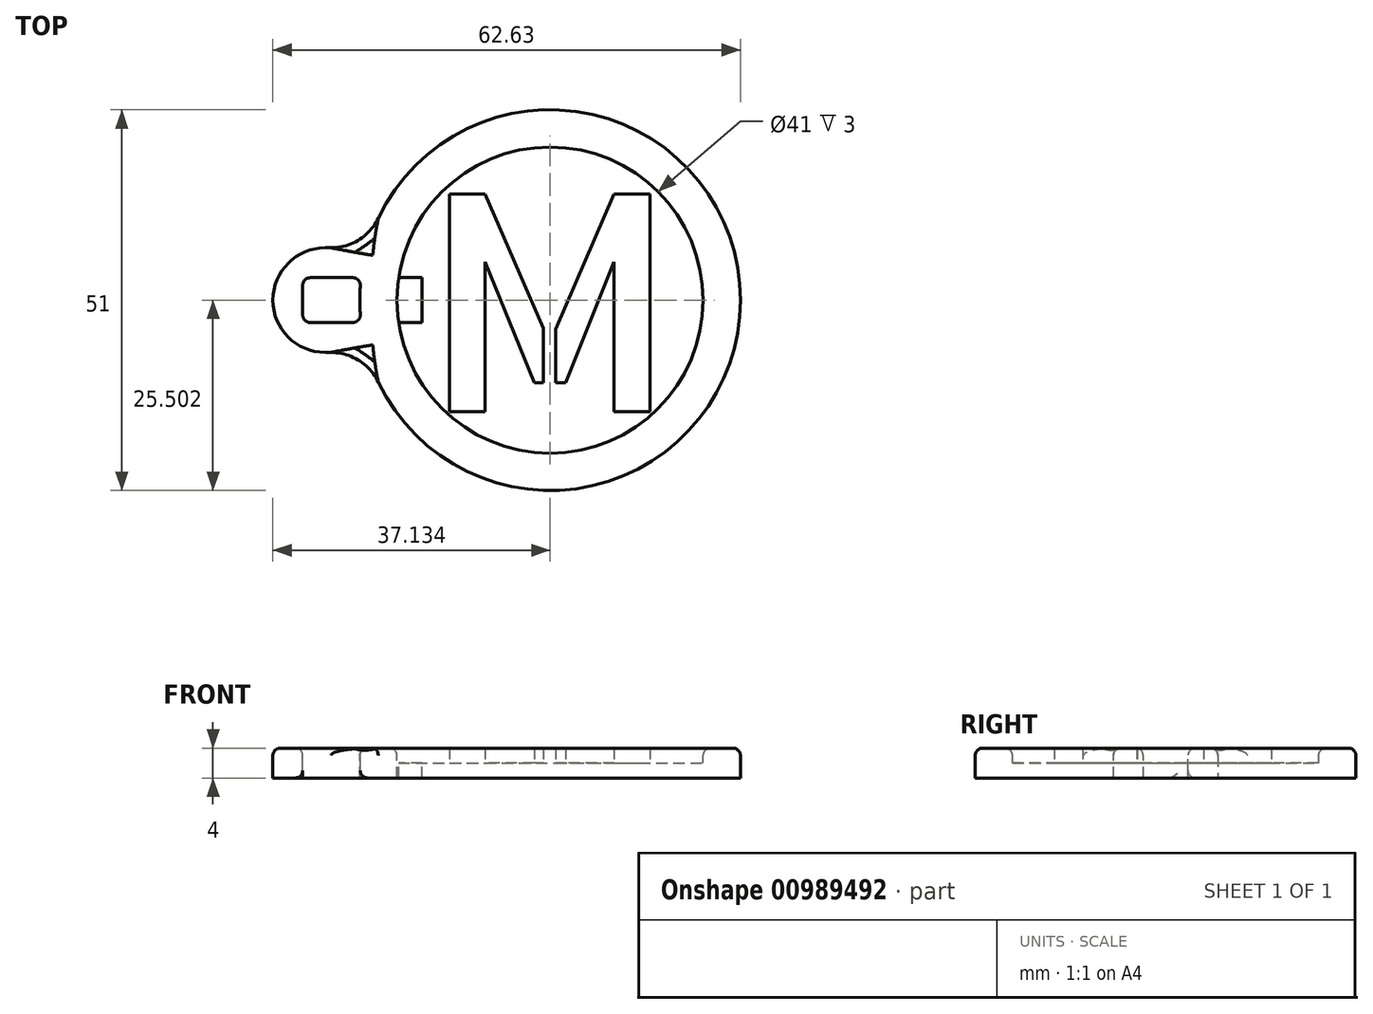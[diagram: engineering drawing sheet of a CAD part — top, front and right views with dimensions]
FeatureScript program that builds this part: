
annotation { "Feature Type Name" : "Feature", "Feature Type Description" : "" }
export const myFeature = defineFeature(function(context is Context, id is Id, definition is map)
    precondition{}
    {
        {
            var Q0;
            Q0=qCreatedBy(makeId("Top.planeOp"),FACE);
            var sketch = newSketch(context, id + "F0", { "sketchPlane" : qUnion([Q0])});
            skText(sketch, "E0", { "text": "M", "fontName": "AllertaStencil-Regular.ttf"});
            skCircle(sketch, "E1", {"center": v(17.13, 14.92) * mm, "radius": 20.5 * mm});
            skPoint(sketch, "E1.centerSnap0", {"position": v(16.61, 14.92) * mm});
            skCircle(sketch, "E2", {"center": v(17.13, 14.92) * mm, "radius": 25.5 * mm});
            skLineSegment(sketch, "E3.bottom", {"start": v(0, 7.92) * mm, "end": v(-20, 7.92) * mm});
            skLineSegment(sketch, "E3.top", {"start": v(0, 21.92) * mm, "end": v(-20, 21.92) * mm});
            skLineSegment(sketch, "E3.left", {"start": v(0, 7.92) * mm, "end": v(0, 21.92) * mm});
            skLineSegment(sketch, "E3.right", {"start": v(-20, 7.92) * mm, "end": v(-20, 21.92) * mm});
            skLineSegment(sketch, "E4.bottom", {"start": v(0, 11.92) * mm, "end": v(-16, 11.92) * mm});
            skLineSegment(sketch, "E4.top", {"start": v(0, 17.92) * mm, "end": v(-16, 17.92) * mm});
            skLineSegment(sketch, "E4.left", {"start": v(0, 11.92) * mm, "end": v(0, 17.92) * mm});
            skLineSegment(sketch, "E4.right", {"start": v(-16, 11.92) * mm, "end": v(-16, 17.92) * mm});
            const initialGuessF0  = {"E0": [0, 0, 1, 0, 0.02911]};
            skSetInitialGuess(sketch, initialGuessF0);
            skSolve(sketch);
        }
        {
            var Q0;
            {var subQ0=sQuery(id+"F0.wireOp",EDGE,"E3.top");var subQ1=sQuery(id+"F0.wireOp",EDGE,"E1");var subQ2=makeQuery(id+"F0.imprint","INTERSECT",VERTEX,{"derivedFrom":[subQ1,subQ0]});Q0=makeQuery(id+"F0.imprint","IMPRINT",FACE,{"disambiguationData":[TD([[makeQuery(id+"F0.imprint","IMPRINT",EDGE,{"disambiguationData":[TD([[subQ2,1.0]])],"derivedFrom":subQ1}),-1.0]])]});}
            var Q1;
            {var subQ0=sQuery(id+"F0.wireOp",EDGE,"E4.top");var subQ1=sQuery(id+"F0.wireOp",EDGE,"E1");var subQ2=makeQuery(id+"F0.imprint","INTERSECT",VERTEX,{"derivedFrom":[subQ1,subQ0]});Q1=makeQuery(id+"F0.imprint","IMPRINT",FACE,{"disambiguationData":[TD([[makeQuery(id+"F0.imprint","IMPRINT",EDGE,{"disambiguationData":[TD([[subQ2,1.0]])],"derivedFrom":subQ1}),-1.0]])]});}
            var Q2;
            {var subQ0=sQuery(id+"F0.wireOp",EDGE,"E4.top");var subQ1=sQuery(id+"F0.wireOp",EDGE,"E1");var subQ2=makeQuery(id+"F0.imprint","INTERSECT",VERTEX,{"derivedFrom":[subQ1,subQ0]});Q2=makeQuery(id+"F0.imprint","IMPRINT",FACE,{"disambiguationData":[TD([[makeQuery(id+"F0.imprint","IMPRINT",EDGE,{"disambiguationData":[TD([[subQ2,-1.0]])],"derivedFrom":subQ1}),-1.0]])]});}
            var Q3;
            {var subQ0=sQuery(id+"F0.wireOp",EDGE,"E4.bottom");var subQ1=sQuery(id+"F0.wireOp",EDGE,"E1");var subQ2=makeQuery(id+"F0.imprint","INTERSECT",VERTEX,{"derivedFrom":[subQ1,subQ0]});Q3=makeQuery(id+"F0.imprint","IMPRINT",FACE,{"disambiguationData":[TD([[makeQuery(id+"F0.imprint","IMPRINT",EDGE,{"disambiguationData":[TD([[subQ2,-1.0]])],"derivedFrom":subQ1}),-1.0]])]});}
            var Q4;
            {var subQ0=sQuery(id+"F0.wireOp",EDGE,"E3.right");Q4=makeQuery(id+"F0.imprint","IMPRINT",FACE,{"disambiguationData":[TD([[makeQuery(id+"F0.imprint","IMPRINT",EDGE,{"derivedFrom":subQ0}),-1.0]])]});}
            var Q5;
            {var subQ5=sQuery(id+"F0.wireOp",EDGE,"E4.left");Q5=makeQuery(id+"F0.imprint","IMPRINT",FACE,{"disambiguationData":[TD([[makeQuery(id+"F0.imprint","IMPRINT",EDGE,{"derivedFrom":subQ5}),1.0]])]});}
            var Q6;
            {var subQ0=sQuery(id+"F0.wireOp",EDGE,"E4.top");var subQ1=sQuery(id+"F0.wireOp",EDGE,"E1");var subQ2=makeQuery(id+"F0.imprint","INTERSECT",VERTEX,{"derivedFrom":[subQ1,subQ0]});Q6=makeQuery(id+"F0.imprint","IMPRINT",FACE,{"disambiguationData":[TD([[makeQuery(id+"F0.imprint","IMPRINT",EDGE,{"disambiguationData":[TD([[subQ2,1.0]])],"derivedFrom":subQ1}),1.0]])]});}
            var Q7;
            {var subQ0=sQuery(id+"F0.wireOp",EDGE,"E4.bottom");var subQ1=sQuery(id+"F0.wireOp",EDGE,"E1");var subQ2=makeQuery(id+"F0.imprint","INTERSECT",VERTEX,{"derivedFrom":[subQ1,subQ0]});Q7=makeQuery(id+"F0.imprint","IMPRINT",FACE,{"disambiguationData":[TD([[makeQuery(id+"F0.imprint","IMPRINT",EDGE,{"disambiguationData":[TD([[subQ2,-1.0]])],"derivedFrom":subQ1}),1.0]])]});}
            var Q8;
            Q8=makeQuery(id+"F0.imprint","IMPRINT",FACE,{"disambiguationData":[TD([[makeQuery(id+"F0.imprint","IMPRINT",EDGE,{"derivedFrom":sQuery(id+"F0.wireOp",EDGE,"E0.sketch_text.stroke-0")}),1.0]])]});
            var Q9;
            Q9=makeQuery(id+"F0.imprint","IMPRINT",FACE,{"disambiguationData":[TD([[makeQuery(id+"F0.imprint","IMPRINT",EDGE,{"derivedFrom":sQuery(id+"F0.wireOp",EDGE,"E0.sketch_text.stroke-0")}),-1.0]])]});
            var Q10;
            Q10=makeQuery(id+"F0.imprint","IMPRINT",FACE,{"disambiguationData":[TD([[makeQuery(id+"F0.imprint","IMPRINT",EDGE,{"derivedFrom":sQuery(id+"F0.wireOp",EDGE,"E0.sketch_text.stroke-8")}),-1.0]])]});
            var Q11;
            {var subQ0=sQuery(id+"F0.wireOp",EDGE,"wxvuEN93-N0YH-PEau-rIz5-DYCHeZqUycJo");var subQ1=sQuery(id+"F0.wireOp",EDGE,"E1");var subQ2=makeQuery(id+"F0.imprint","INTERSECT",VERTEX,{"derivedFrom":[subQ1,subQ0]});Q11=makeQuery(id+"F0.imprint","IMPRINT",FACE,{"disambiguationData":[TD([[makeQuery(id+"F0.imprint","IMPRINT",EDGE,{"disambiguationData":[TD([[subQ2,-1.0]])],"derivedFrom":subQ1}),-1.0]])]});}
            var Q12;
            {var subQ4=sQuery(id+"F0.wireOp",EDGE,"E0.sketch_text.stroke-2");Q12=makeQuery(id+"F0.imprint","IMPRINT",FACE,{"disambiguationData":[TD([[makeQuery(id+"F0.imprint","IMPRINT",EDGE,{"derivedFrom":subQ4}),-1.0]])]});}
            var Q13;
            {var subQ0=sQuery(id+"F0.wireOp",EDGE,"E0.sketch_text.stroke-5");var subQ1=sQuery(id+"F0.wireOp",EDGE,"E0.sketch_text.stroke-4");var subQ2=makeQuery(id+"F0.imprint","INTERSECT",VERTEX,{"derivedFrom":[subQ1,subQ0]});Q13=makeQuery(id+"F0.imprint","IMPRINT",FACE,{"disambiguationData":[TD([[makeQuery(id+"F0.imprint","IMPRINT",EDGE,{"disambiguationData":[TD([[subQ2,1.0]])],"derivedFrom":subQ1}),1.0]])]});}
            var Q14;
            {var subQ5=sQuery(id+"F0.wireOp",EDGE,"E0.sketch_text.stroke-6");var subQ7=sQuery(id+"F0.wireOp",EDGE,"E0.sketch_text.stroke-5");var subQ8=makeQuery(id+"F0.imprint","INTERSECT",VERTEX,{"derivedFrom":[subQ7,subQ5]});Q14=makeQuery(id+"F0.imprint","IMPRINT",FACE,{"disambiguationData":[TD([[makeQuery(id+"F0.imprint","IMPRINT",EDGE,{"disambiguationData":[TD([[subQ8,1.0]])],"derivedFrom":subQ7}),-1.0]])]});}
            var Q15;
            {var subQ5=sQuery(id+"F0.wireOp",EDGE,"E1");var subQ7=sQuery(id+"F0.wireOp",EDGE,"E0.sketch_text.stroke-7");var subQ8=makeQuery(id+"F0.imprint","INTERSECT",VERTEX,{"derivedFrom":[subQ7,subQ5]});Q15=makeQuery(id+"F0.imprint","IMPRINT",FACE,{"disambiguationData":[TD([[makeQuery(id+"F0.imprint","IMPRINT",EDGE,{"disambiguationData":[TD([[subQ8,-1.0]])],"derivedFrom":subQ7}),1.0]])]});}
            extrude(context, id + "F1", {"entities" : qUnion([Q0, Q1, Q2, Q3, Q4, Q5, Q6, Q7, Q8, Q9, Q10, Q11, Q12, Q13, Q14, Q15]), "oppositeDirection" : true, "depth" : 2 * mm, "offsetDistance" : 25 * mm});
        }
        {
            var Q0;
            Q0=makeQuery(id+"F0.imprint","IMPRINT",FACE,{"disambiguationData":[TD([[makeQuery(id+"F0.imprint","IMPRINT",EDGE,{"derivedFrom":sQuery(id+"F0.wireOp",EDGE,"E0.sketch_text.stroke-8")}),-1.0]])]});
            var Q1;
            Q1=makeQuery(id+"F0.imprint","IMPRINT",FACE,{"disambiguationData":[TD([[makeQuery(id+"F0.imprint","IMPRINT",EDGE,{"derivedFrom":sQuery(id+"F0.wireOp",EDGE,"E0.sketch_text.stroke-0")}),-1.0]])]});
            var Q2;
            {var subQ0=sQuery(id+"F0.wireOp",EDGE,"E3.top");var subQ1=sQuery(id+"F0.wireOp",EDGE,"E1");var subQ2=makeQuery(id+"F0.imprint","INTERSECT",VERTEX,{"derivedFrom":[subQ1,subQ0]});Q2=makeQuery(id+"F0.imprint","IMPRINT",FACE,{"disambiguationData":[TD([[makeQuery(id+"F0.imprint","IMPRINT",EDGE,{"disambiguationData":[TD([[subQ2,1.0]])],"derivedFrom":subQ1}),-1.0]])]});}
            var Q3;
            {var subQ0=sQuery(id+"F0.wireOp",EDGE,"E4.top");var subQ1=sQuery(id+"F0.wireOp",EDGE,"E1");var subQ2=makeQuery(id+"F0.imprint","INTERSECT",VERTEX,{"derivedFrom":[subQ1,subQ0]});Q3=makeQuery(id+"F0.imprint","IMPRINT",FACE,{"disambiguationData":[TD([[makeQuery(id+"F0.imprint","IMPRINT",EDGE,{"disambiguationData":[TD([[subQ2,1.0]])],"derivedFrom":subQ1}),-1.0]])]});}
            var Q4;
            {var subQ0=sQuery(id+"F0.wireOp",EDGE,"E4.top");var subQ1=sQuery(id+"F0.wireOp",EDGE,"E1");var subQ2=makeQuery(id+"F0.imprint","INTERSECT",VERTEX,{"derivedFrom":[subQ1,subQ0]});Q4=makeQuery(id+"F0.imprint","IMPRINT",FACE,{"disambiguationData":[TD([[makeQuery(id+"F0.imprint","IMPRINT",EDGE,{"disambiguationData":[TD([[subQ2,-1.0]])],"derivedFrom":subQ1}),-1.0]])]});}
            var Q5;
            {var subQ0=sQuery(id+"F0.wireOp",EDGE,"E4.bottom");var subQ1=sQuery(id+"F0.wireOp",EDGE,"E1");var subQ2=makeQuery(id+"F0.imprint","INTERSECT",VERTEX,{"derivedFrom":[subQ1,subQ0]});Q5=makeQuery(id+"F0.imprint","IMPRINT",FACE,{"disambiguationData":[TD([[makeQuery(id+"F0.imprint","IMPRINT",EDGE,{"disambiguationData":[TD([[subQ2,-1.0]])],"derivedFrom":subQ1}),-1.0]])]});}
            var Q6;
            {var subQ0=sQuery(id+"F0.wireOp",EDGE,"E3.right");Q6=makeQuery(id+"F0.imprint","IMPRINT",FACE,{"disambiguationData":[TD([[makeQuery(id+"F0.imprint","IMPRINT",EDGE,{"derivedFrom":subQ0}),-1.0]])]});}
            extrude(context, id + "F2", {"entities" : qUnion([Q0, Q1, Q2, Q3, Q4, Q5, Q6]), "operationType" : NewBodyOperationType.ADD, "depth" : 2 * mm, "offsetDistance" : 25 * mm});
        }
        {
            var Q0;
            Q0=makeQuery(id+"F2.opExtrude","CAP_FACE",FACE,{"disambiguationData":[OSD([sQuery(id+"F0.wireOp",EDGE,"E1"),sQuery(id+"F0.wireOp",EDGE,"E2"),sQuery(id+"F0.wireOp",EDGE,"E3.bottom"),sQuery(id+"F0.wireOp",EDGE,"E3.top"),sQuery(id+"F0.wireOp",EDGE,"E3.right"),sQuery(id+"F0.wireOp",EDGE,"E4.bottom"),sQuery(id+"F0.wireOp",EDGE,"E4.top"),sQuery(id+"F0.wireOp",EDGE,"E4.right")])],"isStart":false});
            var Q1;
            Q1=makeQuery(id+"F2.opExtrude","CAP_EDGE",EDGE,{"disambiguationData":[OSD([sQuery(id+"F0.wireOp",EDGE,"E4.top")])],"isStart":false});
            var Q2;
            {var subQ0=sQuery(id+"F0.wireOp",EDGE,"E4.top");Q2=makeQuery(id+"F2.boolean.opBoolean","MERGE",FACE,{"derivedFrom":[makeQuery(id+"F1.opExtrude","SWEPT_FACE",FACE,{"disambiguationData":[OSD([subQ0])]}),makeQuery(id+"F2.opExtrude","SWEPT_FACE",FACE,{"disambiguationData":[OSD([subQ0])]})]});}
            var Q3;
            {var subQ0=sQuery(id+"F0.wireOp",EDGE,"E4.bottom");var subQ1=sQuery(id+"F0.wireOp",EDGE,"E2");Q3=makeQuery(id+"F2.boolean.opBoolean","MERGE",EDGE,{"derivedFrom":[makeQuery(id+"F1.opExtrude","SWEPT_EDGE",EDGE,{"disambiguationData":[OSD([subQ1,subQ0])]}),makeQuery(id+"F2.opExtrude","SWEPT_EDGE",EDGE,{"disambiguationData":[OSD([subQ1,subQ0])]})]});}
            var Q4;
            {var subQ0=sQuery(id+"F0.wireOp",EDGE,"E4.right");var subQ1=sQuery(id+"F0.wireOp",EDGE,"E4.bottom");Q4=makeQuery(id+"F2.boolean.opBoolean","MERGE",EDGE,{"derivedFrom":[makeQuery(id+"F1.opExtrude","SWEPT_EDGE",EDGE,{"disambiguationData":[OSD([subQ1,subQ0])]}),makeQuery(id+"F2.opExtrude","SWEPT_EDGE",EDGE,{"disambiguationData":[OSD([subQ1,subQ0])]})]});}
            fillet(context, id + "F3", {"entities" : qUnion([Q0, Q1, Q2, Q3, Q4]), "radius" : 1 * mm, "tangentPropagation" : true, "allowEdgeOverflow" : false});
        }
        {
            var Q0;
            {var subQ0=sQuery(id+"F0.wireOp",EDGE,"E3.right");var subQ1=sQuery(id+"F0.wireOp",EDGE,"E3.bottom");Q0=makeQuery(id+"F2.boolean.opBoolean","MERGE",EDGE,{"derivedFrom":[makeQuery(id+"F1.opExtrude","SWEPT_EDGE",EDGE,{"disambiguationData":[OSD([subQ1,subQ0])]}),makeQuery(id+"F2.opExtrude","SWEPT_EDGE",EDGE,{"disambiguationData":[OSD([subQ1,subQ0])]})]});}
            var Q1;
            {var subQ0=sQuery(id+"F0.wireOp",EDGE,"E3.right");var subQ1=sQuery(id+"F0.wireOp",EDGE,"E3.top");Q1=makeQuery(id+"F2.boolean.opBoolean","MERGE",EDGE,{"derivedFrom":[makeQuery(id+"F1.opExtrude","SWEPT_EDGE",EDGE,{"disambiguationData":[OSD([subQ1,subQ0])]}),makeQuery(id+"F2.opExtrude","SWEPT_EDGE",EDGE,{"disambiguationData":[OSD([subQ1,subQ0])]})]});}
            var Q2;
            {var subQ0=sQuery(id+"F0.wireOp",EDGE,"E3.top");var subQ1=sQuery(id+"F0.wireOp",EDGE,"E2");Q2=makeQuery(id+"F2.boolean.opBoolean","MERGE",EDGE,{"derivedFrom":[makeQuery(id+"F1.opExtrude","SWEPT_EDGE",EDGE,{"disambiguationData":[OSD([subQ1,subQ0])]}),makeQuery(id+"F2.opExtrude","SWEPT_EDGE",EDGE,{"disambiguationData":[OSD([subQ1,subQ0])]})]});}
            var Q3;
            {var subQ0=sQuery(id+"F0.wireOp",EDGE,"E3.bottom");var subQ1=sQuery(id+"F0.wireOp",EDGE,"E2");Q3=makeQuery(id+"F2.boolean.opBoolean","MERGE",EDGE,{"derivedFrom":[makeQuery(id+"F1.opExtrude","SWEPT_EDGE",EDGE,{"disambiguationData":[OSD([subQ1,subQ0])]}),makeQuery(id+"F2.opExtrude","SWEPT_EDGE",EDGE,{"disambiguationData":[OSD([subQ1,subQ0])]})]});}
            fillet(context, id + "F4", {"entities" : qUnion([Q0, Q1, Q2, Q3]), "radius" : 7 * mm, "tangentPropagation" : true, "allowEdgeOverflow" : false});
        }
    });
